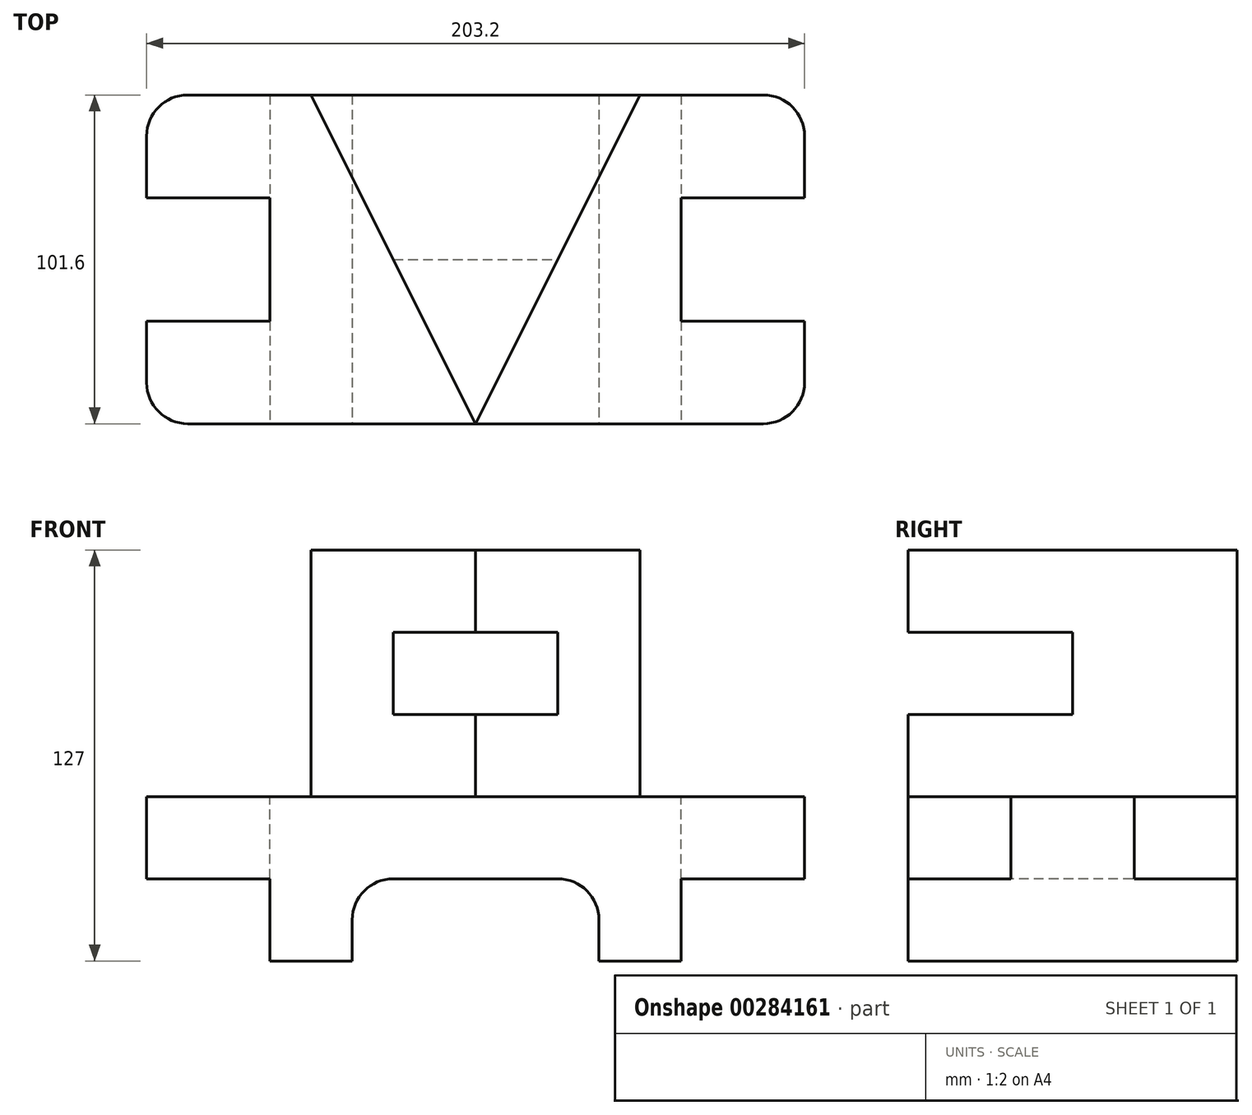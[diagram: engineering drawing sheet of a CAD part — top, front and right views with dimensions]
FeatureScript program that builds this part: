
annotation { "Feature Type Name" : "Feature", "Feature Type Description" : "" }
export const myFeature = defineFeature(function(context is Context, id is Id, definition is map)
    precondition{}
    {
        {
            var Q0;
            Q0=qCreatedBy(makeId("Front.planeOp"),FACE);
            var sketch = newSketch(context, id + "F0", { "sketchPlane" : qUnion([Q0])});
            skLineSegment(sketch, "E0", {"start": v(-101.6, 0) * mm, "end": v(101.6, 0) * mm});
            skLineSegment(sketch, "E1", {"start": v(101.6, 0) * mm, "end": v(101.6, -25.4) * mm});
            skLineSegment(sketch, "E2", {"start": v(101.6, -25.4) * mm, "end": v(63.5, -25.4) * mm});
            skLineSegment(sketch, "E3", {"start": v(63.5, -25.4) * mm, "end": v(63.5, -50.8) * mm});
            skLineSegment(sketch, "E4", {"start": v(63.5, -50.8) * mm, "end": v(38.1, -50.8) * mm});
            skLineSegment(sketch, "E5", {"start": v(38.1, -50.8) * mm, "end": v(38.1, -25.4) * mm});
            skLineSegment(sketch, "E6", {"start": v(38.1, -25.4) * mm, "end": v(-38.1, -25.4) * mm});
            skLineSegment(sketch, "E7", {"start": v(-38.1, -25.4) * mm, "end": v(-38.1, -50.8) * mm});
            skLineSegment(sketch, "E8", {"start": v(-38.1, -50.8) * mm, "end": v(-63.5, -50.8) * mm});
            skLineSegment(sketch, "E9", {"start": v(-63.5, -50.8) * mm, "end": v(-63.5, -25.4) * mm});
            skLineSegment(sketch, "E10", {"start": v(-63.5, -25.4) * mm, "end": v(-101.6, -25.4) * mm});
            skLineSegment(sketch, "E11", {"start": v(-101.6, -25.4) * mm, "end": v(-101.6, 0) * mm});
            skSolve(sketch);
        }
        {
            var Q0;
            Q0=makeQuery(id+"F0.imprint","IMPRINT",FACE,{"disambiguationData":[TD([[makeQuery(id+"F0.imprint","IMPRINT",EDGE,{"derivedFrom":sQuery(id+"F0.wireOp",EDGE,"E0")}),-1.0]])]});
            extrude(context, id + "F1", {"entities" : qUnion([Q0]), "endBound" : BoundingType.SYMMETRIC, "oppositeDirection" : true, "depth" : 101.6 * mm});
        }
        {
            var Q0;
            Q0=makeQuery(id+"F1.opExtrude","SWEPT_FACE",FACE,{"disambiguationData":[OSD([sQuery(id+"F0.wireOp",EDGE,"E0")])]});
            var sketch = newSketch(context, id + "F2", { "sketchPlane" : qUnion([Q0])});
            skLineSegment(sketch, "E12", {"start": v(-101.6, 19.05) * mm, "end": v(-63.5, 19.05) * mm});
            skLineSegment(sketch, "E13", {"start": v(-63.5, 19.05) * mm, "end": v(-63.5, -19.05) * mm});
            skLineSegment(sketch, "E14", {"start": v(-63.5, -19.05) * mm, "end": v(-101.6, -19.05) * mm});
            skLineSegment(sketch, "E15", {"start": v(101.6, 19.05) * mm, "end": v(63.5, 19.05) * mm});
            skLineSegment(sketch, "E16", {"start": v(63.5, 19.05) * mm, "end": v(63.5, -19.05) * mm});
            skLineSegment(sketch, "E17", {"start": v(63.5, -19.05) * mm, "end": v(101.6, -19.05) * mm});
            skLineSegment(sketch, "E18", {"start": v(-50.8, 50.8) * mm, "end": v(0, -50.8) * mm});
            skLineSegment(sketch, "E19", {"start": v(0, -50.8) * mm, "end": v(50.8, 50.8) * mm});
            skLineSegment(sketch, "E20", {"start": v(-50.8, 50.8) * mm, "end": v(50.8, 50.8) * mm});
            skSolve(sketch);
        }
        {
            var Q0;
            Q0=makeQuery(id+"F2.imprint","IMPRINT",FACE,{"disambiguationData":[TD([[makeQuery(id+"F2.imprint","IMPRINT",EDGE,{"derivedFrom":sQuery(id+"F2.wireOp",EDGE,"E18")}),1.0]])]});
            extrude(context, id + "F3", {"entities" : qUnion([Q0]), "operationType" : NewBodyOperationType.ADD, "depth" : 76.2 * mm});
        }
        {
            var Q0;
            {var subQ0=sQuery(id+"F2.wireOp",EDGE,"E15");Q0=makeQuery(id+"F2.imprint","IMPRINT",FACE,{"disambiguationData":[TD([[makeQuery(id+"F2.imprint","IMPRINT",EDGE,{"derivedFrom":subQ0}),1.0]])]});}
            var Q1;
            {var subQ0=sQuery(id+"F2.wireOp",EDGE,"E12");Q1=makeQuery(id+"F2.imprint","IMPRINT",FACE,{"disambiguationData":[TD([[makeQuery(id+"F2.imprint","IMPRINT",EDGE,{"derivedFrom":subQ0}),-1.0]])]});}
            extrude(context, id + "F4", {"entities" : qUnion([Q0, Q1]), "operationType" : NewBodyOperationType.REMOVE, "endBound" : BoundingType.THROUGH_ALL, "oppositeDirection" : true, "depth" : 25.4 * mm});
        }
        {
            var Q0;
            Q0=makeQuery(id+"F1.opExtrude","CAP_FACE",FACE,{"disambiguationData":[OSD([sQuery(id+"F0.wireOp",EDGE,"E0"),sQuery(id+"F0.wireOp",EDGE,"E1"),sQuery(id+"F0.wireOp",EDGE,"E2"),sQuery(id+"F0.wireOp",EDGE,"E3"),sQuery(id+"F0.wireOp",EDGE,"E4"),sQuery(id+"F0.wireOp",EDGE,"E5"),sQuery(id+"F0.wireOp",EDGE,"E6"),sQuery(id+"F0.wireOp",EDGE,"E7"),sQuery(id+"F0.wireOp",EDGE,"E8"),sQuery(id+"F0.wireOp",EDGE,"E9"),sQuery(id+"F0.wireOp",EDGE,"E10"),sQuery(id+"F0.wireOp",EDGE,"E11")])],"isStart":true});
            var sketch = newSketch(context, id + "F5", { "sketchPlane" : qUnion([Q0])});
            skLineSegment(sketch, "E21", {"start": v(-25.4, 50.8) * mm, "end": v(25.4, 50.8) * mm});
            skLineSegment(sketch, "E22", {"start": v(25.4, 50.8) * mm, "end": v(25.4, 25.4) * mm});
            skLineSegment(sketch, "E23", {"start": v(25.4, 25.4) * mm, "end": v(-25.4, 25.4) * mm});
            skLineSegment(sketch, "E24", {"start": v(-25.4, 25.4) * mm, "end": v(-25.4, 50.8) * mm});
            skSolve(sketch);
        }
        {
            var Q0;
            Q0=makeQuery(id+"F5.imprint","IMPRINT",FACE,{"disambiguationData":[TD([[makeQuery(id+"F5.imprint","IMPRINT",EDGE,{"derivedFrom":sQuery(id+"F5.wireOp",EDGE,"E21")}),-1.0]])]});
            extrude(context, id + "F6", {"entities" : qUnion([Q0]), "operationType" : NewBodyOperationType.REMOVE, "oppositeDirection" : true, "depth" : 50.8 * mm});
        }
        {
            var Q0;
            Q0=makeQuery(id+"F1.opExtrude","CAP_EDGE",EDGE,{"disambiguationData":[OSD([sQuery(id+"F0.wireOp",EDGE,"E1")])],"isStart":true});
            var Q1;
            Q1=makeQuery(id+"F1.opExtrude","CAP_EDGE",EDGE,{"disambiguationData":[OSD([sQuery(id+"F0.wireOp",EDGE,"E1")])],"isStart":false});
            var Q2;
            Q2=makeQuery(id+"F1.opExtrude","CAP_EDGE",EDGE,{"disambiguationData":[OSD([sQuery(id+"F0.wireOp",EDGE,"E11")])],"isStart":false});
            var Q3;
            Q3=makeQuery(id+"F1.opExtrude","CAP_EDGE",EDGE,{"disambiguationData":[OSD([sQuery(id+"F0.wireOp",EDGE,"E11")])],"isStart":true});
            fillet(context, id + "F7", {"entities" : qUnion([Q0, Q1, Q2, Q3]), "radius" : 12.7 * mm, "tangentPropagation" : true, "allowEdgeOverflow" : false});
        }
        {
            var Q0;
            Q0=makeQuery(id+"F1.opExtrude","SWEPT_EDGE",EDGE,{"disambiguationData":[OSD([sQuery(id+"F0.wireOp",EDGE,"E6"),sQuery(id+"F0.wireOp",EDGE,"E7")])]});
            var Q1;
            Q1=makeQuery(id+"F1.opExtrude","SWEPT_EDGE",EDGE,{"disambiguationData":[OSD([sQuery(id+"F0.wireOp",EDGE,"E5"),sQuery(id+"F0.wireOp",EDGE,"E6")])]});
            fillet(context, id + "F8", {"entities" : qUnion([Q0, Q1]), "radius" : 12.7 * mm, "tangentPropagation" : true, "allowEdgeOverflow" : false});
        }
    });
